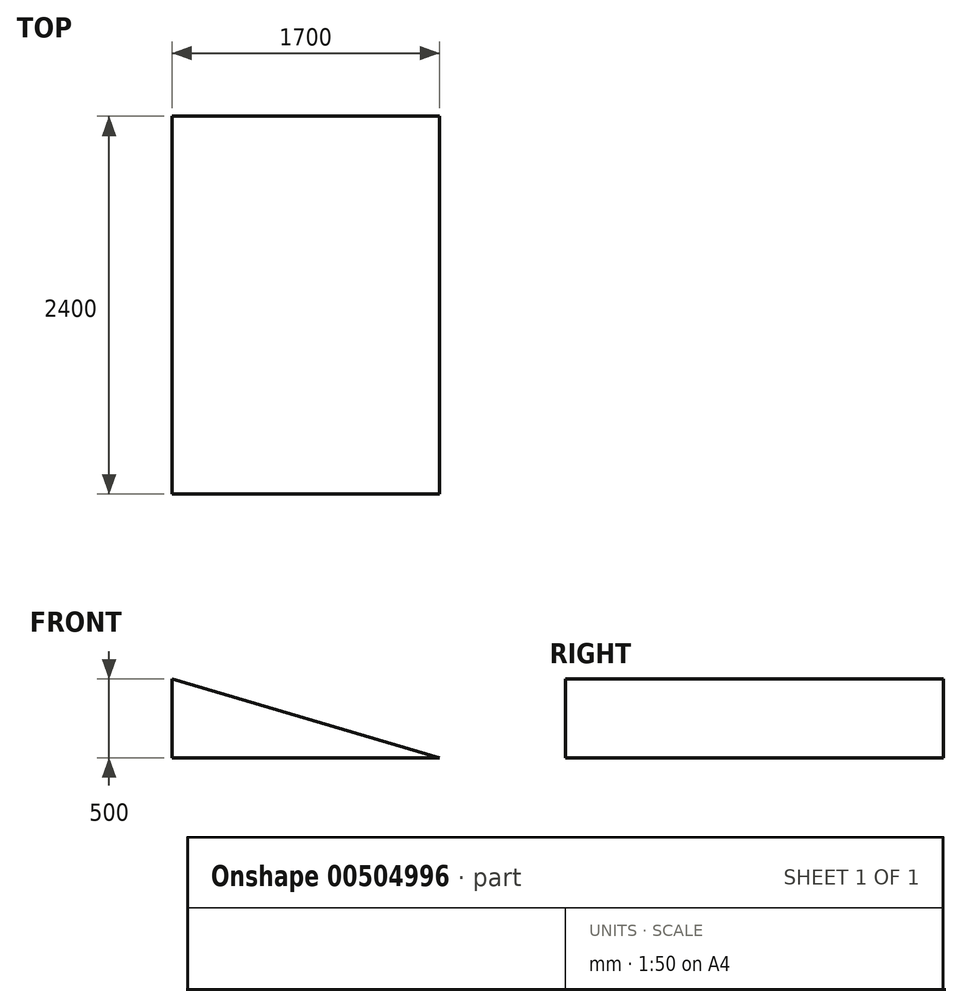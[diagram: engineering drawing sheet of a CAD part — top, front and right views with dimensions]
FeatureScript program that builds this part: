
annotation { "Feature Type Name" : "Feature", "Feature Type Description" : "" }
export const myFeature = defineFeature(function(context is Context, id is Id, definition is map)
    precondition{}
    {
        {
            var Q0;
            Q0=qCreatedBy(makeId("Front.planeOp"),FACE);
            var sketch = newSketch(context, id + "F0", { "sketchPlane" : qUnion([Q0])});
            skLineSegment(sketch, "E0", {"start": v(819.7, 0) * mm, "end": v(-880.3, 500) * mm});
            skLineSegment(sketch, "E1", {"start": v(-880.3, 500) * mm, "end": v(-880.3, 0) * mm});
            skLineSegment(sketch, "E2", {"start": v(-880.3, 0) * mm, "end": v(819.7, 0) * mm});
            skSolve(sketch);
        }
        {
            var Q0;
            Q0=makeQuery(id+"F0.imprint","IMPRINT",FACE,{"disambiguationData":[TD([[makeQuery(id+"F0.imprint","IMPRINT",EDGE,{"derivedFrom":sQuery(id+"F0.wireOp",EDGE,"E0")}),1.0]])]});
            extrude(context, id + "F1", {"entities" : qUnion([Q0]), "depth" : 2400 * mm});
        }
    });
